# Revit family: Batidora_B-30_GENERADO
name_source: partatom
category: Equipos especializados
units: mm (PartAtom-declared; Revit-internal decimal feet)

## family parameters
Compartido = No
Corte con vacíos al cargar = No
Cota de conector redondo = Diámetro de uso
Número OmniClass = 23.21.21.31.11
Punto de cálculo de habitación = No
Se basa en plano de trabajo = No
Siempre vertical = Sí
Tipo de pieza = Normal

## types (7) — shared parameters
Cycle = 50 Hz
Fabricante = SAMMIC S.L.
Foodservice Equipment Identifier = Sí
HP = 0.54
Phase = 1
Revision Code = 1
URL = https://www.sammic.com
URL Cutsheet = http://www.sammic.com
Watts = 400 W
zero-valued in all types: Elevación por defecto

## per-type parameters (varying)
| type | Comentarios de tipo | Conn Plug | FL Amps | Modelo | Specification by Manufacturer | Volts | Weight in Pounds |
| Immersion blender & whisk combo MB-31 230/50-60/1 | Professional hand blender and beater. 400 W. | EU (SCHUKO 2P) | 2 A | 3030676 | · Variable speed motor block.
· 306 mm detachable mixer arm designed for continuous use in recipients of up to 30 l.
· Whisk with capacity for 2 to 50 egg whites. | 230 V | 10.2 |
| Immersion blender & whisk combo MB-31 120/50-60/1 MX | Professional hand blender and beater. 400 W. | USA (NEMA 5-15P / 2P+G) | 4 A | 3030800 | · Variable speed motor block.
· 306 mm detachable mixer arm designed for continuous use in recipients of up to 30 l.
· Whisk with capacity for 2 to 50 egg whites. | 120 V | 10.2 |
| Immersion blender & whisk combo MB-31 230/50-60/1 AUS | Professional hand blender and beater. 400 W. | AU/NZ (AS 3112 10A / 2P) | 2 A | 3030798 | · Variable speed motor block.
· 306 mm detachable mixer arm designed for continuous use in recipients of up to 30 l.
· Whisk with capacity for 2 to 50 egg whites. | 230 V | 10.2 |
| Immersion blender & whisk combo MB-31 120/50-60/1 USA | Professional hand blender and beater. 400 W. | USA (NEMA 5-15P / 2P+G) | 4 A | 3030801 | · Variable speed motor block.
· 306 mm detachable mixer arm designed for continuous use in recipients of up to 30 l.
· Whisk with capacity for 2 to 50 egg whites. | 120 V | 10.2 |
| Whisk B-30 230/50-60/1 | Professional beater. 400 W. | EU (SCHUKO 2P) | 2 A | 3030669 | · Variable speed motor block.
· Whisk with capacity for 2 to 50 egg whites. | 230 V | 7.7 |
| Whisk B-30 230/50-60/1 AUS | Professional beater. 400 W. | AU/NZ (AS 3112 10A / 2P) | 2 A | 3030804 | · Variable speed motor block.
· Whisk with capacity for 2 to 50 egg whites. | 230 V | 7.7 |
| Whisk B-30 120/50-60/1 USA | Professional beater. 400 W. | USA (NEMA 5-15P / 2P+G) | 4 A | 3030807 | · Variable speed motor block.
· Whisk with capacity for 2 to 50 egg whites. | 120 V | 7.7 |

note: column(s) folded — value = type name in every type: Descripción
